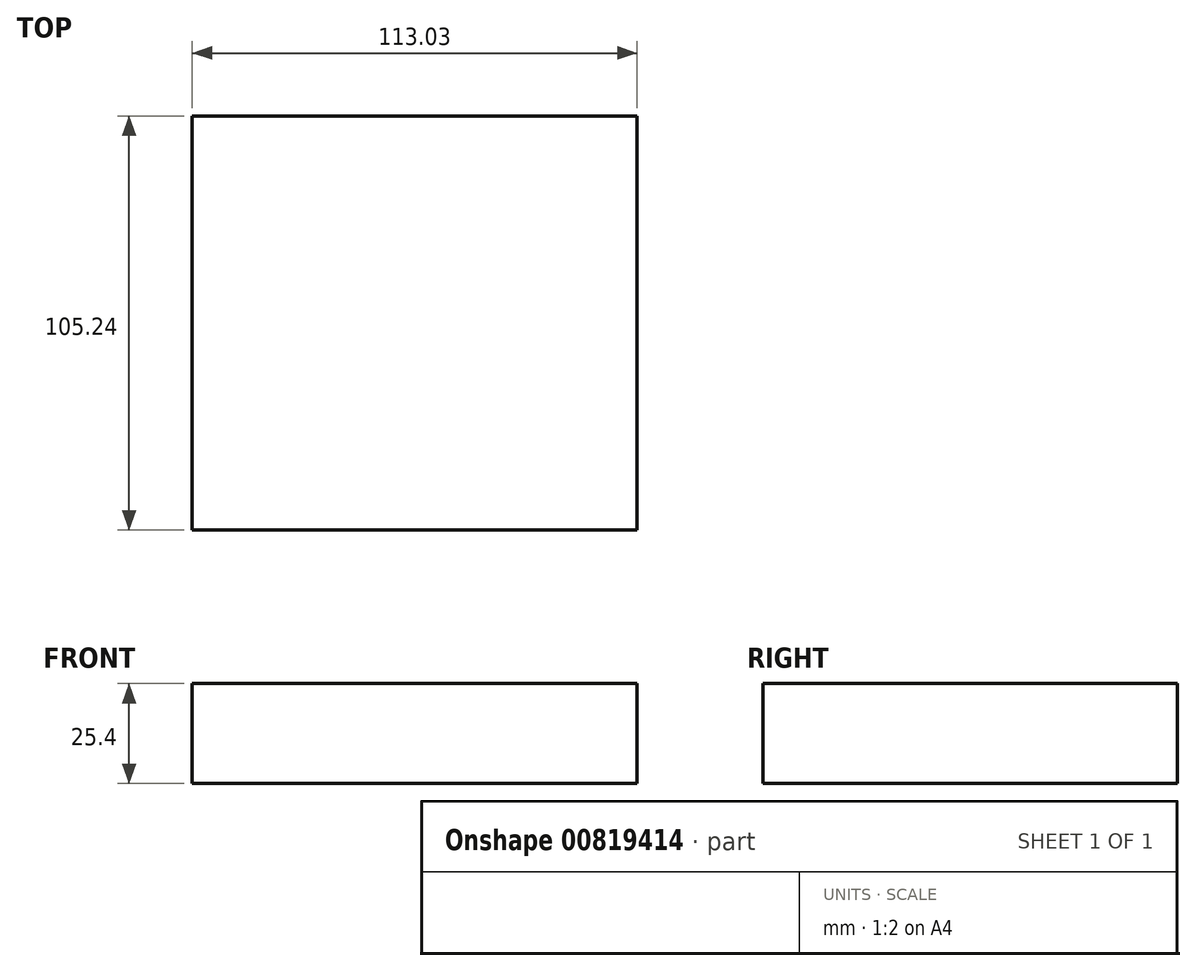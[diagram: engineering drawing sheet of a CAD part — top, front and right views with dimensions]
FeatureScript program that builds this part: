
annotation { "Feature Type Name" : "Feature", "Feature Type Description" : "" }
export const myFeature = defineFeature(function(context is Context, id is Id, definition is map)
    precondition{}
    {
        {
            var Q0;
            Q0=qCreatedBy(makeId("Top.planeOp"),FACE);
            var sketch = newSketch(context, id + "F0", { "sketchPlane" : qUnion([Q0])});
            skLineSegment(sketch, "E0.bottom", {"start": v(0, 0) * mm, "end": v(113.03, 0) * mm});
            skLineSegment(sketch, "E0.top", {"start": v(0, 105.24) * mm, "end": v(113.03, 105.24) * mm});
            skLineSegment(sketch, "E0.left", {"start": v(0, 0) * mm, "end": v(0, 105.24) * mm});
            skLineSegment(sketch, "E0.right", {"start": v(113.03, 0) * mm, "end": v(113.03, 105.24) * mm});
            skSolve(sketch);
        }
        {
            var Q0;
            Q0=makeQuery(id+"F0.imprint","IMPRINT",FACE,{"disambiguationData":[TD([[makeQuery(id+"F0.imprint","IMPRINT",EDGE,{"derivedFrom":sQuery(id+"F0.wireOp",EDGE,"E0.bottom")}),1.0]])]});
            extrude(context, id + "F1", {"entities" : qUnion([Q0]), "depth" : 25.4 * mm, "offsetDistance" : 25.4 * mm});
        }
    });
